# Revit family: 712-0065-04-201-DN125
name_source: partatom
category: Pipe Fittings
units: mm (PartAtom-declared; Revit-internal decimal feet)

## family parameters
Always vertical = Yes
Cut with Voids When Loaded = No
Part Type = Elbow
Round Connector Dimension = Use Diameter
Shared = No
Work Plane-Based = No

## types (1)
- DN100_PN10/16
    Body_wallthickness = 140 mm  [stored 0.459318 ft]
    DN 25_PN10/16 = 712-0125-04-201
    DN125_PN10/16 = Yes
    Description_ = AVK FLANGED PIPE W/LOOSE FLANGES
    FOD = 125 mm  [stored 0.410105 ft]
    Flange_thickness = 19 mm
    ID(Radius) = 63 mm
    L = 150 mm  [stored 0.492126 ft]
    L_Ref = 90 mm  [stored 0.295276 ft]
    Nominal Diameter(DN) = 125 mm  [stored 0.410105 ft]
    RF_Thick = 3 mm  [stored 0.00984252 ft]
    Rf_Dia = 92 mm  [stored 0.301837 ft]
    Search_Table = 712-0420-001-DN40-300
    URL product pages = https://www.avkvalves.com

note: [stored X ft] marks values corroborated as IEEE doubles in the binary element streams (Revit-internal decimal feet)

## geometry (parser evidence)
native form markers: Sweep x6
no freeform markers — native parametric forms only
